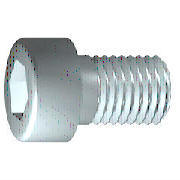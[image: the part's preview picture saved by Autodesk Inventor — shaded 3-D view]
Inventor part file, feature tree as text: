
AUTODESK INVENTOR PART (.ipt)
format: ipt  version: 2023.3 (Build 273359000, 359)  size: 192,000 bytes
history: native  units: mm (DEFAULTED — no unit token found)
features: sketch x2, other x1, extrude x1, plane x1, fillet x1
ambient origin geometry x7: Origin, YZ Plane, XY Plane, X Axis, Y Axis, Z Axis, Center Point
bodies: Solid1 (feature_tree)
feature tree (6):
  other  "Körper"
  extrude  "Loch"  Depth=3.0mm
  plane  "Work Plane1"
  fillet  "Fillet2"  Radius=3.0mm
  sketch  "Skizze1"  dims[d1=10.75mm d2=0.306825mm d3=3.0mm]
  sketch  "Skizze2"  dims[d4=1.3mm d5=60.0deg d6=3.0mm d7=3.0mm d8=2.886751mm d9=5.5mm d10=90.0deg d11=10.0mm d12=0.0mm d13=10.75mm d14=0.0mm d15=0.306725mm d16=0.306725mm d17=0.3mm d19=0.0mm d26=12.0mm d27=45.0deg d28=0.0mm d29=0.0mm d30=0.1mm]
